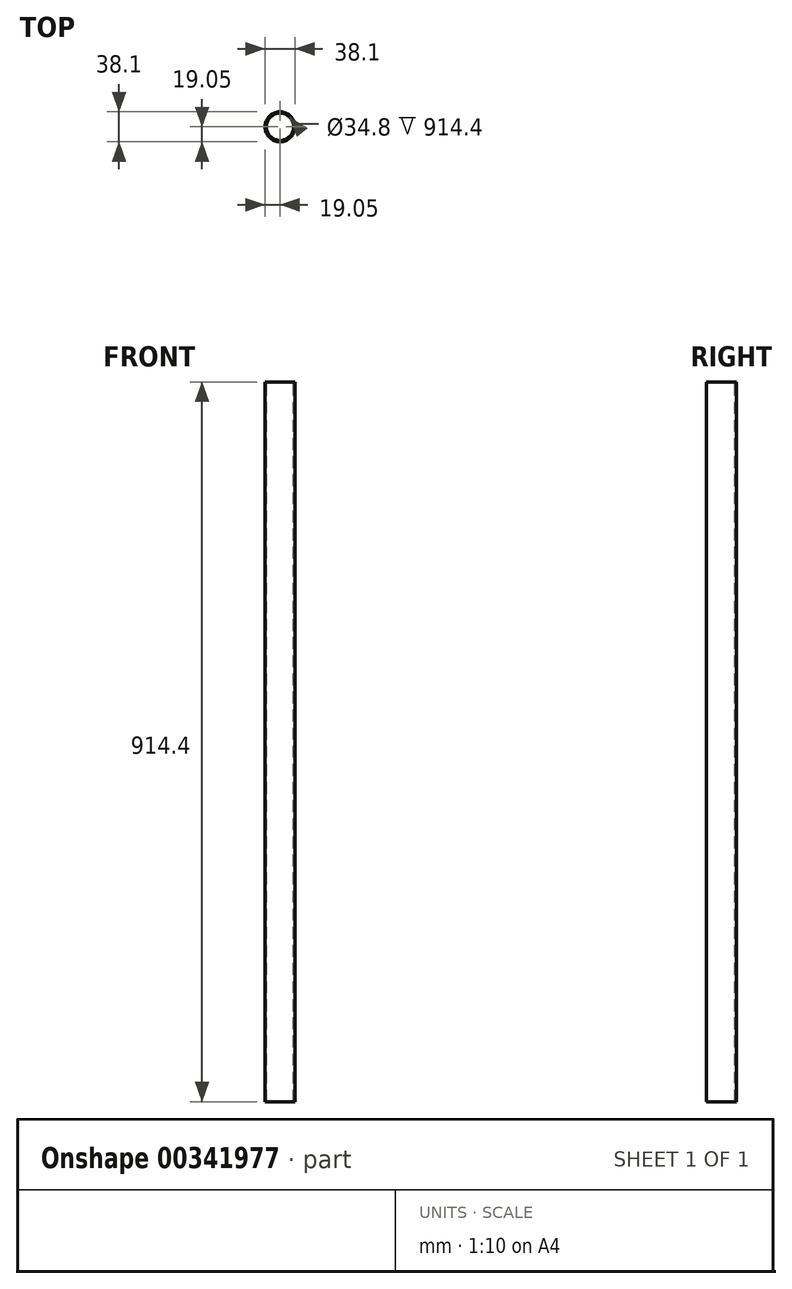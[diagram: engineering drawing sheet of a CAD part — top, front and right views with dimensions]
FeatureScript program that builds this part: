
annotation { "Feature Type Name" : "Feature", "Feature Type Description" : "" }
export const myFeature = defineFeature(function(context is Context, id is Id, definition is map)
    precondition{}
    {
        {
            var Q0;
            Q0=qCreatedBy(makeId("Top.planeOp"),FACE);
            var sketch = newSketch(context, id + "F0", { "sketchPlane" : qUnion([Q0])});
            skCircle(sketch, "E0", {"center": v(0, 0) * mm, "radius": 19.05 * mm});
            skSolve(sketch);
        }
        {
            var Q0;
            Q0=makeQuery(id+"F0.imprint","IMPRINT",FACE,{"disambiguationData":[TD([[makeQuery(id+"F0.imprint","IMPRINT",EDGE,{"derivedFrom":sQuery(id+"F0.wireOp",EDGE,"E0")}),1.0]])]});
            extrude(context, id + "F1", {"entities" : qUnion([Q0]), "depth" : 914.4 * mm});
        }
        {
            var Q0;
            Q0=makeQuery(id+"F1.opExtrude","CAP_FACE",FACE,{"disambiguationData":[OSD([sQuery(id+"F0.wireOp",EDGE,"E0")])],"isStart":false});
            var sketch = newSketch(context, id + "F2", { "sketchPlane" : qUnion([Q0])});
            skCircle(sketch, "E1", {"center": v(0, 0) * mm, "radius": 17.4 * mm});
            skSolve(sketch);
        }
        {
            var Q0;
            Q0=sQuery(id+"F2.wireOp",VERTEX,"E1.center");
            var Q1;
            Q1=makeQuery(id+"F1.opExtrude","SWEPT_BODY",BODY,{"disambiguationData":[OSD([sQuery(id+"F0.wireOp",EDGE,"E0")])]});
            hole(context, id + "F3", {"style" : HoleStyle.SIMPLE, "endStyle" : HoleEndStyle.THROUGH, "holeDiameter" : 34.8 * mm, "isTappedThrough" : true, "tappedDepth" : 12.7 * mm, "tapClearance" : 3, "locations" : qUnion([Q0]), "scope" : qUnion([Q1])});
        }
        {
            var Q0;
            Q0=qCreatedBy(makeId("Front.planeOp"),FACE);
            var sketch = newSketch(context, id + "F4", { "sketchPlane" : qUnion([Q0])});
            skCircle(sketch, "E2", {"center": v(0, 539.94) * mm, "radius": 17.03 * mm});
            skSolve(sketch);
        }
        {
            var Q0;
            Q0=sQuery(id+"F4.wireOp",EDGE,"E2");
            extrude(context, id + "F5", {"bodyType" : ToolBodyType.SURFACE, "surfaceEntities" : qUnion([Q0]), "depth" : 609.6 * mm});
        }
    });
